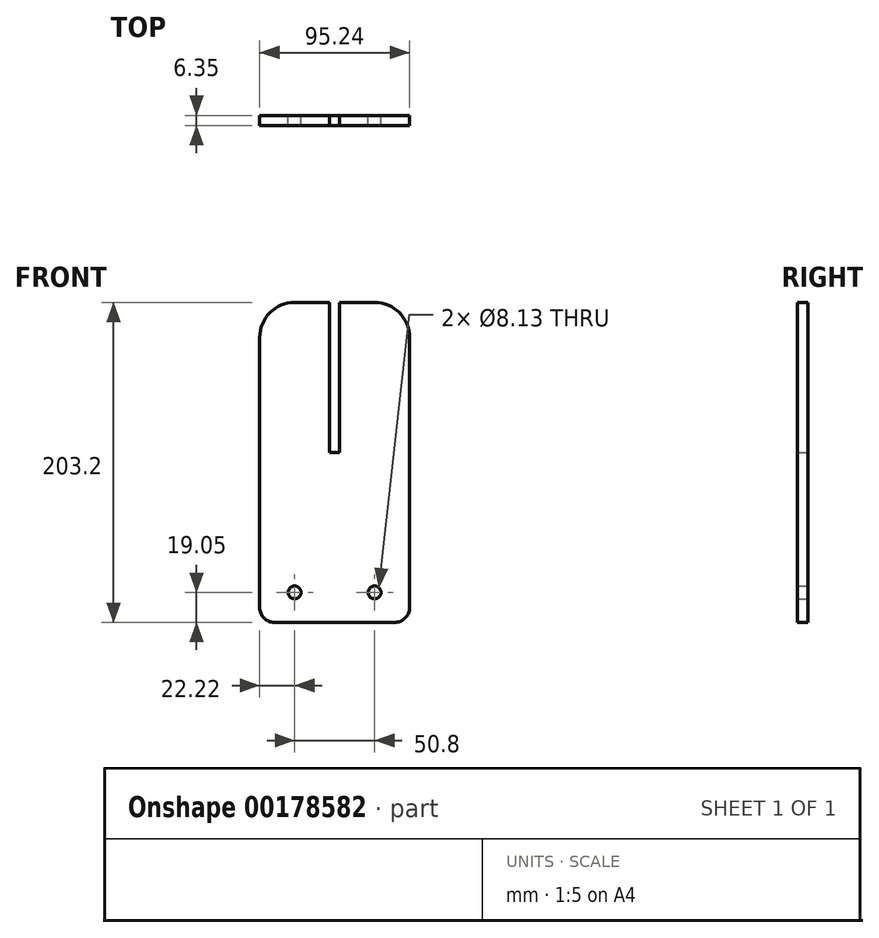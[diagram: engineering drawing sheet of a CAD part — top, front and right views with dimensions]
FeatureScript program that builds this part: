
annotation { "Feature Type Name" : "Feature", "Feature Type Description" : "" }
export const myFeature = defineFeature(function(context is Context, id is Id, definition is map)
    precondition{}
    {
        {
            var Q0;
            Q0=qCreatedBy(makeId("Front.planeOp"),FACE);
            var sketch = newSketch(context, id + "F0", { "sketchPlane" : qUnion([Q0])});
            skLineSegment(sketch, "E0.bottom", {"start": v(38.1, -101.6) * mm, "end": v(-38.1, -101.6) * mm});
            skLineSegment(sketch, "E0.top", {"start": v(25.4, 101.6) * mm, "end": v(3.18, 101.6) * mm});
            skLineSegment(sketch, "E0.left", {"start": v(47.63, -92.07) * mm, "end": v(47.63, 79.37) * mm});
            skLineSegment(sketch, "E0.right", {"start": v(-47.63, -92.08) * mm, "end": v(-47.62, 79.37) * mm});
            skPoint(sketch, "E0.middle", {"position": v(0, 0) * mm});
            skPoint(sketch, "E1.visualSharp", {"position": v(-47.62, 101.6) * mm});
            skArc(sketch, "E1.filletArc", {"start": v(-25.4, 101.6) * mm, "mid": v(-41.12, 95.1) * mm, "end": v(-47.62, 79.37) * mm});
            skPoint(sketch, "E2.visualSharp", {"position": v(47.63, 101.6) * mm});
            skArc(sketch, "E2.filletArc", {"start": v(47.63, 79.37) * mm, "mid": v(41.12, 95.1) * mm, "end": v(25.4, 101.6) * mm});
            skPoint(sketch, "E3.visualSharp", {"position": v(-47.63, -101.6) * mm});
            skArc(sketch, "E3.filletArc", {"start": v(-47.63, -92.08) * mm, "mid": v(-44.84, -98.81) * mm, "end": v(-38.1, -101.6) * mm});
            skPoint(sketch, "E4.visualSharp", {"position": v(47.62, -101.6) * mm});
            skArc(sketch, "E4.filletArc", {"start": v(38.1, -101.6) * mm, "mid": v(44.84, -98.81) * mm, "end": v(47.63, -92.07) * mm});
            skLineSegment(sketch, "E5", {"start": v(0, 0) * mm, "end": v(0, 106.63) * mm, "construction": true});
            skLineSegment(sketch, "E6.0", {"start": v(3.18, 6.35) * mm, "end": v(3.18, 101.6) * mm});
            skLineSegment(sketch, "E7.0", {"start": v(-3.18, 6.35) * mm, "end": v(-3.18, 101.6) * mm});
            skLineSegment(sketch, "E8", {"start": v(-3.18, 6.35) * mm, "end": v(3.18, 6.35) * mm});
            skLineSegment(sketch, "E9.trimOffspring", {"start": v(-3.18, 101.6) * mm, "end": v(-25.4, 101.6) * mm});
            skCircle(sketch, "E10", {"center": v(-25.4, -82.55) * mm, "radius": 4.06 * mm});
            skCircle(sketch, "E11.MirrorC", {"center": v(25.4, -82.55) * mm, "radius": 4.06 * mm});
            skSolve(sketch);
        }
        {
            var Q0;
            Q0=qSketchRegion(id+"F0",true);
            extrude(context, id + "F1", {"entities" : qUnion([Q0]), "depth" : 6.35 * mm});
        }
    });
